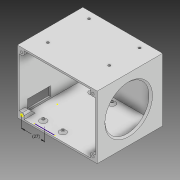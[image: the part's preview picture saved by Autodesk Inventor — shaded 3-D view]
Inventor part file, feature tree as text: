
AUTODESK INVENTOR PART (.ipt)
format: ipt  version: 2020 (Build 240168000, 168)  size: 309,760 bytes
history: native  units: mm
features: sketch x11, extrude x9, other x5, chamfer x2, projected_geometry x2, revolve x1, fillet x1
ambient origin geometry x8: Origin, YZ Plane, XZ Plane, XY Plane, X Axis, Y Axis, Z Axis, Center Point
bodies: Solid1 (feature_tree)
feature tree (31):
  other  "Blocks"
  extrude  "Extrusion1"  Depth=90.0mm
  extrude  "Extrusion2"  Depth=2.0mm TaperAngle=0.0deg
  revolve  "Revolution1"  [1 undecoded]
  extrude  "Extrusion3"  Depth=40.0mm
  extrude  "Extrusion4"  TaperAngle=90.0deg  [1 undecoded]
  extrude  "Extrusion5"  Depth=3.0mm
  extrude  "Extrusion6"  Depth=72.0mm TaperAngle=0.0deg
  chamfer  "Chamfer1"  Distance=2.0mm
  extrude  "Extrusion7"  Depth=6.0mm
  extrude  "Extrusion8"  Depth=45.0mm
  extrude  "Extrusion9"  Depth=72.0mm TaperAngle=0.0deg
  chamfer  "Chamfer2"  Distance=8.0mm
  fillet  "Fillet1"  Radius=2.0mm
  sketch  "Sketch11"  dims[d39=15.0mm d40=45.0mm d41=72.0mm d42=0.0mm d43=8.0mm d44=2.0mm d45=0.0mm d46=11.0mm d47=27.0mm d48=2.0mm d49=0.0mm d51=19.0mm d52=9.0mm d53=12.0mm d54=2.0mm d55=0.0mm d56=2.8mm d57=6.0mm d58=6.0mm d59=6.0mm d60=6.0mm d61=13.0mm d62=0.0mm d63=6.0mm d64=2.0mm d65=45.0deg d66=2.0mm d67=27.0mm]
  sketch  "Sketch1"  dims[d0=70.0mm d1=90.0mm]
  sketch  "Sketch2"  dims[d2=2.0mm d3=2.0mm d4=0.0mm]
  projected_geometry  "Projected Loop1"
  sketch  "Sketch3"  dims[d5=2.0mm d6=75.0mm d7=0.0mm]
  sketch  "Sketch4"  dims[d8=40.0mm d9=28.0mm]
  other  "Block1"
  sketch  "Sketch5"  dims[d10=45.0deg d11=90.0deg]
  sketch  "Sketch6"  dims[d12=59.5mm d13=66.5mm d14=54.8mm d15=48.5mm d16=16.0mm d17=2.7mm d20=3.0mm]
  other  "Block2"
  sketch  "Sketch7"  dims[d22=10.0mm d23=72.0mm d24=0.0mm]
  sketch  "Sketch8"  dims[d25=8.0mm d26=2.0mm d27=0.0mm]
  sketch  "Sketch9"  dims[d28=2.0mm d29=2.0mm d30=45.0deg]
  sketch  "Sketch10"  dims[d31=23.0mm d32=58.0mm d33=30.0mm d34=65.0mm d35=2.7mm d36=6.0mm d38=3.5mm]
  projected_geometry  "Projected Loop2"
  other  "Block1:1"
  other  "Block2:1"
note: 2 required parameter values undecoded (feature->parameter linkage not recoverable at this tier; creation-order binding heuristic only, values carry confidence <= 0.55)